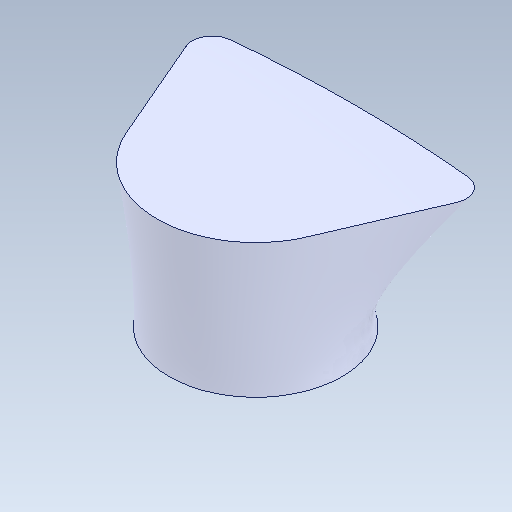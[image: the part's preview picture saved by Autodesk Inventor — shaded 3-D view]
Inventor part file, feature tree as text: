
AUTODESK INVENTOR PART (.ipt)
format: ipt  version: 2021 (Build 250183000, 183)  size: 174,080 bytes
history: mixed  units: in
note: dims shown in document units (in); Inventor stores cm internally (conversion verified against a paired STEP export)
features: loft x1, imported_body x1
ambient origin geometry x8: Origin, YZ Plane, XZ Plane, XY Plane, X Axis, Y Axis, Z Axis, Center Point
bodies: Solid1 (imported_parasolid)
feature tree (2):
  loft  "Loft1"
  imported_body  NMx_Import_Brep_tag  [imported B-rep: ~5 faces, bbox_mm=None]
